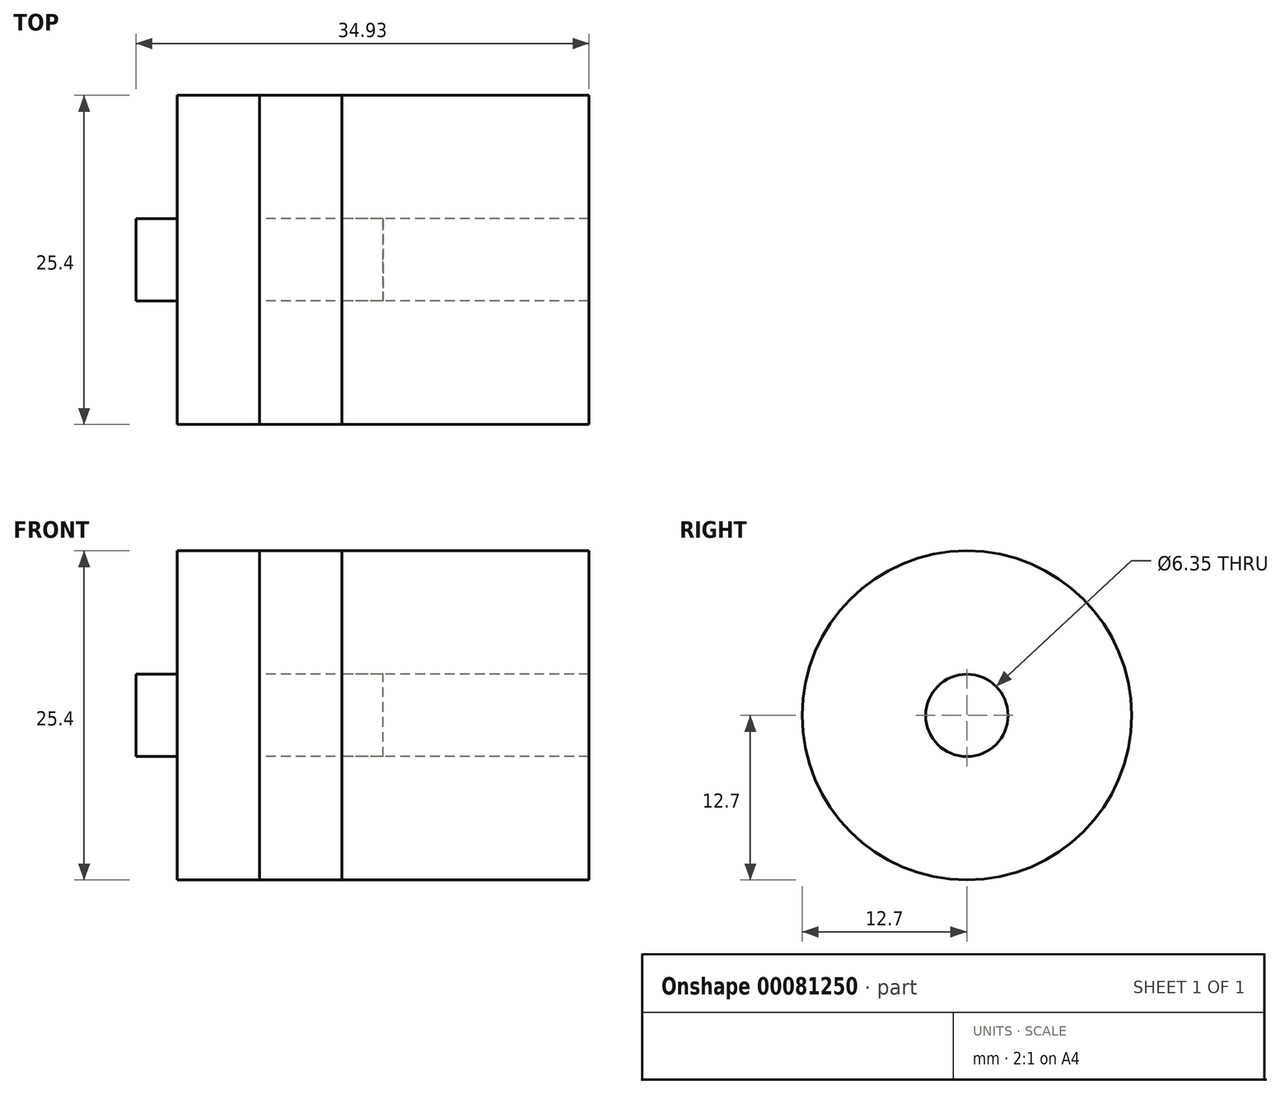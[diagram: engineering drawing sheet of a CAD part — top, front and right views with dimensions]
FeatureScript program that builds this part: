
annotation { "Feature Type Name" : "Feature", "Feature Type Description" : "" }
export const myFeature = defineFeature(function(context is Context, id is Id, definition is map)
    precondition{}
    {
        {
            var Q0;
            Q0=qCreatedBy(makeId("Right.planeOp"),FACE);
            var sketch = newSketch(context, id + "F0", { "sketchPlane" : qUnion([Q0])});
            skCircle(sketch, "E0", {"center": v(0, 0) * mm, "radius": 3.18 * mm});
            skCircle(sketch, "E1", {"center": v(0, 0) * mm, "radius": 12.7 * mm});
            skSolve(sketch);
        }
        {
            var Q0;
            Q0=makeQuery(id+"F0.imprint","IMPRINT",FACE,{"disambiguationData":[TD([[makeQuery(id+"F0.imprint","IMPRINT",EDGE,{"derivedFrom":sQuery(id+"F0.wireOp",EDGE,"E0")}),1.0]])]});
            extrude(context, id + "F1", {"entities" : qUnion([Q0]), "endBound" : BoundingType.SYMMETRIC, "depth" : 19.05 * mm});
        }
        {
            var Q0;
            Q0=makeQuery(id+"F0.imprint","IMPRINT",FACE,{"disambiguationData":[TD([[makeQuery(id+"F0.imprint","IMPRINT",EDGE,{"derivedFrom":sQuery(id+"F0.wireOp",EDGE,"E0")}),-1.0]])]});
            extrude(context, id + "F2", {"entities" : qUnion([Q0]), "operationType" : NewBodyOperationType.ADD, "endBound" : BoundingType.SYMMETRIC, "depth" : 12.7 * mm});
        }
        {
            var Q0;
            Q0 = qSketchRegion(id + "F0", true);
            extrude(context, id + "F3", {"entities" : qUnion([Q0]), "depth" : 25.4 * mm});
        }
    });
